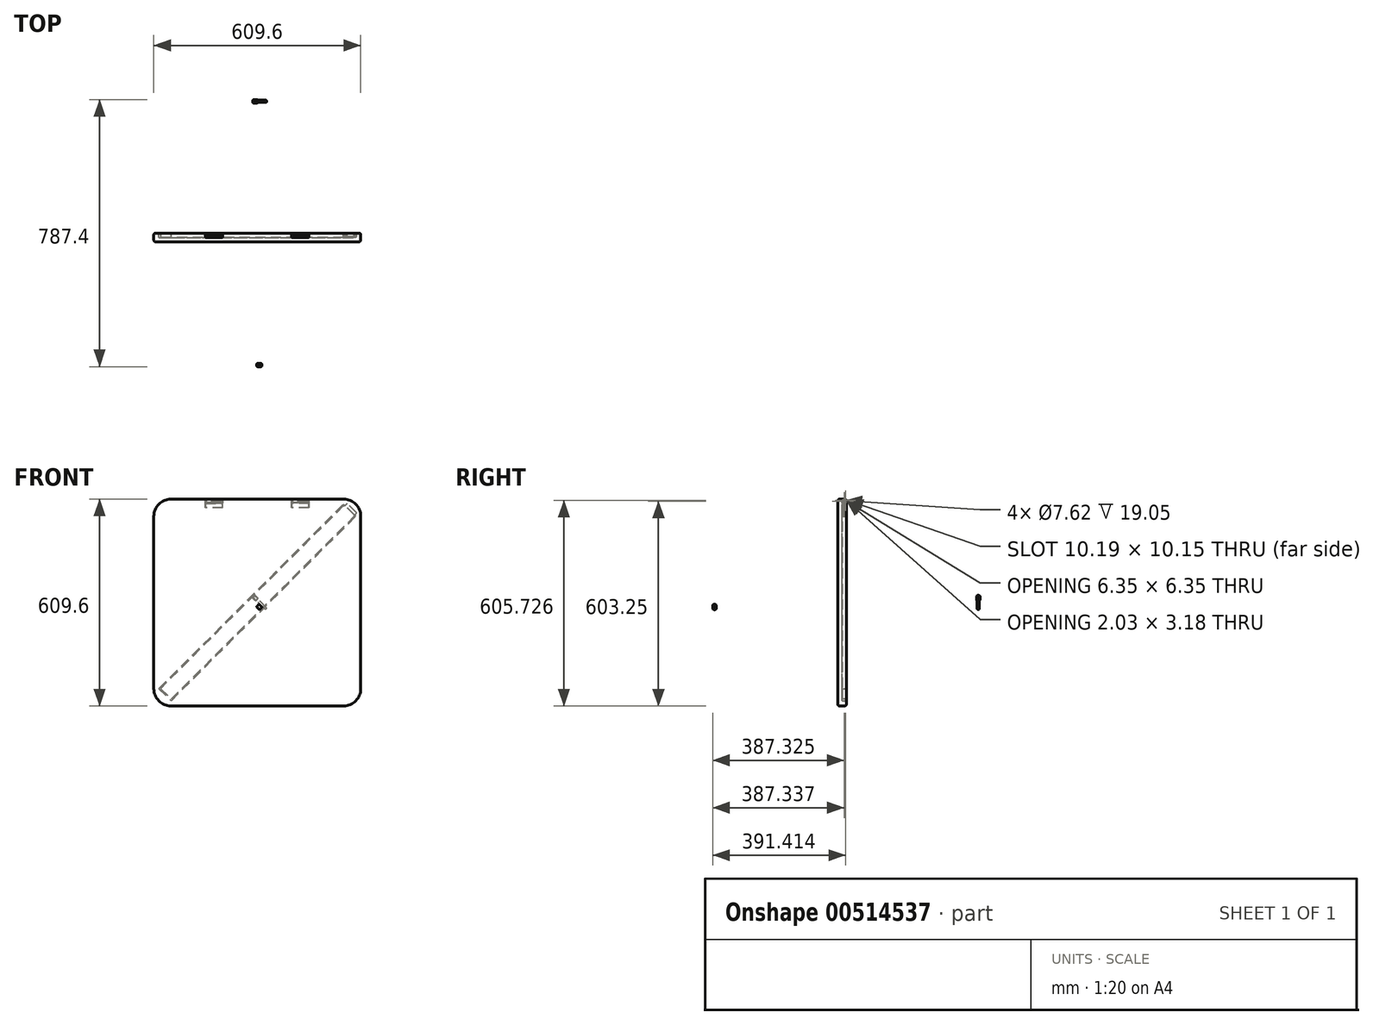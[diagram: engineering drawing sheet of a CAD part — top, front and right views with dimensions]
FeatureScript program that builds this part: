
annotation { "Feature Type Name" : "Feature", "Feature Type Description" : "" }
export const myFeature = defineFeature(function(context is Context, id is Id, definition is map)
    precondition{}
    {
        {
            var Q0;
            Q0=qCreatedBy(makeId("Front.planeOp"),FACE);
            var sketch = newSketch(context, id + "F0", { "sketchPlane" : qUnion([Q0])});
            skLineSegment(sketch, "E0.bottom", {"start": v(304.8, 304.8) * mm, "end": v(-304.8, 304.8) * mm});
            skLineSegment(sketch, "E0.top", {"start": v(304.8, -304.8) * mm, "end": v(-304.8, -304.8) * mm});
            skLineSegment(sketch, "E0.left", {"start": v(304.8, 304.8) * mm, "end": v(304.8, -304.8) * mm});
            skLineSegment(sketch, "E0.right", {"start": v(-304.8, 304.8) * mm, "end": v(-304.8, -304.8) * mm});
            skPoint(sketch, "E0.middle", {"position": v(0, 0) * mm});
            skSolve(sketch);
        }
        {
            var Q0;
            Q0=makeQuery(id+"F0.imprint","IMPRINT",FACE,{"disambiguationData":[TD([[makeQuery(id+"F0.imprint","IMPRINT",EDGE,{"derivedFrom":sQuery(id+"F0.wireOp",EDGE,"E0.bottom")}),1.0]])]});
            extrude(context, id + "F1", {"entities" : qUnion([Q0]), "depth" : 25.4 * mm, "offsetDistance" : 25.4 * mm});
        }
        {
            var Q0;
            Q0=makeQuery(id+"F1.opExtrude","SWEPT_EDGE",EDGE,{"disambiguationData":[OSD([sQuery(id+"F0.wireOp",EDGE,"E0.bottom"),sQuery(id+"F0.wireOp",EDGE,"E0.left")])]});
            var Q1;
            Q1=makeQuery(id+"F1.opExtrude","SWEPT_EDGE",EDGE,{"disambiguationData":[OSD([sQuery(id+"F0.wireOp",EDGE,"E0.bottom"),sQuery(id+"F0.wireOp",EDGE,"E0.right")])]});
            var Q2;
            Q2=makeQuery(id+"F1.opExtrude","SWEPT_EDGE",EDGE,{"disambiguationData":[OSD([sQuery(id+"F0.wireOp",EDGE,"E0.top"),sQuery(id+"F0.wireOp",EDGE,"E0.right")])]});
            var Q3;
            Q3=makeQuery(id+"F1.opExtrude","SWEPT_EDGE",EDGE,{"disambiguationData":[OSD([sQuery(id+"F0.wireOp",EDGE,"E0.top"),sQuery(id+"F0.wireOp",EDGE,"E0.left")])]});
            fillet(context, id + "F2", {"entities" : qUnion([Q0, Q1, Q2, Q3]), "radius" : 50.8 * mm, "tangentPropagation" : true, "allowEdgeOverflow" : false});
        }
        {
            var Q0;
            Q0=makeQuery(id+"F1.opExtrude","SWEPT_FACE",FACE,{"disambiguationData":[OSD([sQuery(id+"F0.wireOp",EDGE,"E0.bottom")])]});
            var sketch = newSketch(context, id + "F3", { "sketchPlane" : qUnion([Q0])});
            skLineSegment(sketch, "E1.bottom", {"start": v(-101.6, 12.7) * mm, "end": v(-152.4, 12.7) * mm});
            skLineSegment(sketch, "E1.top", {"start": v(-101.6, -12.7) * mm, "end": v(-152.4, -12.7) * mm});
            skLineSegment(sketch, "E1.left", {"start": v(-101.6, 12.7) * mm, "end": v(-101.6, -12.7) * mm});
            skLineSegment(sketch, "E1.right", {"start": v(-152.4, 12.7) * mm, "end": v(-152.4, -12.7) * mm});
            skPoint(sketch, "E1.middle", {"position": v(-127, 0) * mm});
            skLineSegment(sketch, "E2", {"start": v(-152.4, 0) * mm, "end": v(-152.4, 0) * mm});
            skLineSegment(sketch, "E3", {"start": v(0, 0) * mm, "end": v(-127, 0) * mm});
            skLineSegment(sketch, "E4", {"start": v(0, 0) * mm, "end": v(127, 0) * mm});
            skLineSegment(sketch, "E5.bottom", {"start": v(152.4, 12.7) * mm, "end": v(101.6, 12.7) * mm});
            skLineSegment(sketch, "E5.top", {"start": v(152.4, -12.7) * mm, "end": v(101.6, -12.7) * mm});
            skLineSegment(sketch, "E5.left", {"start": v(152.4, 12.7) * mm, "end": v(152.4, -12.7) * mm});
            skLineSegment(sketch, "E5.right", {"start": v(101.6, 12.7) * mm, "end": v(101.6, -12.7) * mm});
            skPoint(sketch, "E5.middle", {"position": v(127, 0) * mm});
            skSolve(sketch);
        }
        {
            var Q0;
            {var subQ6=sQuery(id+"F3.wireOp",EDGE,"E1.top");Q0=makeQuery(id+"F3.imprint","IMPRINT",FACE,{"disambiguationData":[TD([[makeQuery(id+"F3.imprint","IMPRINT",EDGE,{"derivedFrom":subQ6}),-1.0]])]});}
            var Q1;
            {var subQ1=sQuery(id+"F3.wireOp",EDGE,"E5.top");Q1=makeQuery(id+"F3.imprint","IMPRINT",FACE,{"disambiguationData":[TD([[makeQuery(id+"F3.imprint","IMPRINT",EDGE,{"derivedFrom":subQ1}),-1.0]])]});}
            extrude(context, id + "F4", {"entities" : qUnion([Q0, Q1]), "operationType" : NewBodyOperationType.REMOVE, "oppositeDirection" : true, "depth" : 12.7 * mm, "offsetDistance" : 25.4 * mm});
        }
        {
            var Q0;
            Q0=makeQuery(id+"F4.boolean.opBoolean","COPY",FACE,{"derivedFrom":makeQuery(id+"F4.opExtrude","SWEPT_FACE",FACE,{"disambiguationData":[OSD([sQuery(id+"F3.wireOp",EDGE,"E1.right")])]})});
            var sketch = newSketch(context, id + "F5", { "sketchPlane" : qUnion([Q0])});
            skLineSegment(sketch, "E6", {"start": v(-12.7, 298.45) * mm, "end": v(-6.38, 298.45) * mm});
            skPoint(sketch, "E6.endSnap0", {"position": v(-6.38, 304.8) * mm});
            skCircle(sketch, "E7", {"center": v(-6.38, 298.45) * mm, "radius": 5.08 * mm});
            skCircle(sketch, "E8", {"center": v(-6.38, 298.45) * mm, "radius": 3.81 * mm});
            skCircle(sketch, "E9", {"center": v(-6.38, 298.45) * mm, "radius": 3.18 * mm});
            skSolve(sketch);
        }
        {
            var Q0;
            Q0=makeQuery(id+"F5.imprint","IMPRINT",FACE,{"disambiguationData":[TD([[makeQuery(id+"F5.imprint","IMPRINT",EDGE,{"derivedFrom":sQuery(id+"F5.wireOp",EDGE,"E9")}),1.0]])]});
            extrude(context, id + "F6", {"entities" : qUnion([Q0]), "operationType" : NewBodyOperationType.ADD, "depth" : 50.8 * mm, "offsetDistance" : 25.4 * mm});
        }
        {
            var Q0;
            Q0=makeQuery(id+"F5.imprint","IMPRINT",FACE,{"disambiguationData":[TD([[makeQuery(id+"F5.imprint","IMPRINT",EDGE,{"derivedFrom":sQuery(id+"F5.wireOp",EDGE,"E7")}),1.0]])]});
            extrude(context, id + "F7", {"entities" : qUnion([Q0]), "operationType" : NewBodyOperationType.ADD, "depth" : 19.05 * mm, "offsetDistance" : 25.4 * mm});
        }
        {
            var Q0;
            Q0=makeQuery(id+"F4.boolean.opBoolean","COPY",FACE,{"derivedFrom":makeQuery(id+"F4.opExtrude","SWEPT_FACE",FACE,{"disambiguationData":[OSD([sQuery(id+"F3.wireOp",EDGE,"E1.left")])]})});
            var sketch = newSketch(context, id + "F8", { "sketchPlane" : qUnion([Q0])});
            skLineSegment(sketch, "E10", {"start": v(0, 298.45) * mm, "end": v(6.38, 298.45) * mm});
            skCircle(sketch, "E11", {"center": v(6.38, 298.45) * mm, "radius": 3.81 * mm});
            skCircle(sketch, "E12", {"center": v(6.38, 298.45) * mm, "radius": 5.08 * mm});
            skSolve(sketch);
        }
        {
            var Q0;
            Q0=makeQuery(id+"F8.imprint","IMPRINT",FACE,{"disambiguationData":[TD([[makeQuery(id+"F8.imprint","IMPRINT",EDGE,{"derivedFrom":sQuery(id+"F8.wireOp",EDGE,"E11")}),-1.0]])]});
            extrude(context, id + "F9", {"entities" : qUnion([Q0]), "operationType" : NewBodyOperationType.ADD, "depth" : 19.05 * mm, "offsetDistance" : 25.4 * mm});
        }
        {
            var Q0;
            Q0=makeQuery(id+"F4.boolean.opBoolean","COPY",FACE,{"derivedFrom":makeQuery(id+"F4.opExtrude","CAP_FACE",FACE,{"disambiguationData":[OSD([sQuery(id+"F0.wireOp",EDGE,"E0.bottom"),sQuery(id+"F3.wireOp",EDGE,"E1.top"),sQuery(id+"F3.wireOp",EDGE,"E1.left"),sQuery(id+"F3.wireOp",EDGE,"E1.right"),sQuery(id+"F3.wireOp",EDGE,"E3")])],"isStart":false})});
            var sketch = newSketch(context, id + "F10", { "sketchPlane" : qUnion([Q0])});
            skLineSegment(sketch, "E13.bottom", {"start": v(-152.4, 0) * mm, "end": v(-101.6, 0) * mm});
            skLineSegment(sketch, "E13.top", {"start": v(-152.4, -1.27) * mm, "end": v(-101.6, -1.27) * mm});
            skLineSegment(sketch, "E13.left", {"start": v(-152.4, 0) * mm, "end": v(-152.4, -1.27) * mm});
            skLineSegment(sketch, "E13.right", {"start": v(-101.6, 0) * mm, "end": v(-101.6, -1.27) * mm});
            skSolve(sketch);
        }
        {
            var Q0;
            Q0=makeQuery(id+"F10.imprint","IMPRINT",FACE,{"disambiguationData":[TD([[makeQuery(id+"F10.imprint","IMPRINT",EDGE,{"derivedFrom":sQuery(id+"F10.wireOp",EDGE,"E13.bottom")}),1.0]])]});
            extrude(context, id + "F11", {"entities" : qUnion([Q0]), "operationType" : NewBodyOperationType.REMOVE, "oppositeDirection" : true, "depth" : 12.7 * mm, "offsetDistance" : 25.4 * mm});
        }
        {
            var Q0;
            Q0=makeQuery(id+"F11.boolean.opBoolean","COPY",FACE,{"derivedFrom":makeQuery(id+"F11.opExtrude","SWEPT_FACE",FACE,{"disambiguationData":[OSD([sQuery(id+"F10.wireOp",EDGE,"E13.top")])]})});
            var sketch = newSketch(context, id + "F12", { "sketchPlane" : qUnion([Q0])});
            skLineSegment(sketch, "E14.bottom", {"start": v(101.85, 279.65) * mm, "end": v(152.15, 279.65) * mm});
            skLineSegment(sketch, "E14.top", {"start": v(101.85, 302.26) * mm, "end": v(152.15, 302.26) * mm});
            skLineSegment(sketch, "E14.left", {"start": v(101.85, 279.65) * mm, "end": v(101.85, 302.26) * mm});
            skLineSegment(sketch, "E14.right", {"start": v(152.15, 279.65) * mm, "end": v(152.15, 302.26) * mm});
            skLineSegment(sketch, "E15", {"start": v(127.47, 279.4) * mm, "end": v(127.47, 279.65) * mm});
            skSolve(sketch);
        }
        {
            var Q0;
            Q0 = qSketchRegion(id + "F12", true);
            extrude(context, id + "F13", {"entities" : qUnion([Q0]), "operationType" : NewBodyOperationType.ADD, "depth" : 1.27 * mm, "offsetDistance" : 25.4 * mm});
        }
        {
            var Q0;
            Q0=makeQuery(id+"F13.opExtrude","CAP_EDGE",EDGE,{"disambiguationData":[OSD([sQuery(id+"F12.wireOp",EDGE,"E14.top")])],"isStart":false});
            fillet(context, id + "F14", {"entities" : qUnion([Q0]), "radius" : 2.54 * mm, "tangentPropagation" : true, "allowEdgeOverflow" : false});
        }
        {
            var Q0;
            Q0=makeQuery(id+"F1.opExtrude","CAP_EDGE",EDGE,{"disambiguationData":[OSD([sQuery(id+"F0.wireOp",EDGE,"E0.right")])],"isStart":true});
            var Q1;
            Q1=makeQuery(id+"F1.opExtrude","CAP_EDGE",EDGE,{"disambiguationData":[OSD([sQuery(id+"F0.wireOp",EDGE,"E0.right")])],"isStart":false});
            var Q2;
            {var subQ0=sQuery(id+"F0.wireOp",EDGE,"E0.right");var subQ1=sQuery(id+"F0.wireOp",EDGE,"E0.bottom");Q2=makeQuery(id+"F2.opFillet","BLEND_EDGE",EDGE,{"blendedFrom":[makeQuery(id+"F1.opExtrude","SWEPT_EDGE",EDGE,{"disambiguationData":[OSD([subQ1,subQ0])]}),makeQuery(id+"F1.opExtrude","CAP_FACE",FACE,{"disambiguationData":[OSD([subQ1,sQuery(id+"F0.wireOp",EDGE,"E0.top"),sQuery(id+"F0.wireOp",EDGE,"E0.left"),subQ0])],"isStart":false})],"blendedInto":[makeQuery(id+"F1.opExtrude","CAP_FACE",FACE,{"disambiguationData":[OSD([subQ1,sQuery(id+"F0.wireOp",EDGE,"E0.top"),sQuery(id+"F0.wireOp",EDGE,"E0.left"),subQ0])],"isStart":false})]});}
            var Q3;
            {var subQ0=sQuery(id+"F0.wireOp",EDGE,"E0.right");var subQ1=sQuery(id+"F0.wireOp",EDGE,"E0.bottom");Q3=makeQuery(id+"F2.opFillet","BLEND_EDGE",EDGE,{"blendedFrom":[makeQuery(id+"F1.opExtrude","SWEPT_EDGE",EDGE,{"disambiguationData":[OSD([subQ1,subQ0])]}),makeQuery(id+"F1.opExtrude","CAP_FACE",FACE,{"disambiguationData":[OSD([subQ1,sQuery(id+"F0.wireOp",EDGE,"E0.top"),sQuery(id+"F0.wireOp",EDGE,"E0.left"),subQ0])],"isStart":true})],"blendedInto":[makeQuery(id+"F1.opExtrude","CAP_FACE",FACE,{"disambiguationData":[OSD([subQ1,sQuery(id+"F0.wireOp",EDGE,"E0.top"),sQuery(id+"F0.wireOp",EDGE,"E0.left"),subQ0])],"isStart":true})]});}
            var Q4;
            {var subQ0=sQuery(id+"F0.wireOp",EDGE,"E0.bottom");Q4=makeQuery(id+"F4.boolean.opBoolean","SPLIT",EDGE,{"disambiguationData":[TD([makeQuery(id+"F4.opExtrude","SWEPT_FACE",FACE,{"disambiguationData":[OSD([sQuery(id+"F3.wireOp",EDGE,"E1.left")])]})])],"derivedFrom":makeQuery(id+"F1.opExtrude","CAP_EDGE",EDGE,{"disambiguationData":[OSD([subQ0])],"isStart":true})});}
            fillet(context, id + "F15", {"entities" : qUnion([Q0, Q1, Q2, Q3, Q4]), "radius" : 5.08 * mm, "tangentPropagation" : true, "allowEdgeOverflow" : false});
        }
        {
            var Q0;
            Q0=makeQuery(id+"F4.boolean.opBoolean","COPY",FACE,{"derivedFrom":makeQuery(id+"F4.opExtrude","SWEPT_FACE",FACE,{"disambiguationData":[OSD([sQuery(id+"F3.wireOp",EDGE,"E5.right")])]})});
            var sketch = newSketch(context, id + "F16", { "sketchPlane" : qUnion([Q0])});
            skLineSegment(sketch, "E16", {"start": v(-12.7, 298.45) * mm, "end": v(-6.38, 298.45) * mm});
            skCircle(sketch, "E17", {"center": v(-6.38, 298.45) * mm, "radius": 5.08 * mm});
            skCircle(sketch, "E18", {"center": v(-6.38, 298.45) * mm, "radius": 3.81 * mm});
            skCircle(sketch, "E19", {"center": v(-6.38, 298.45) * mm, "radius": 3.18 * mm});
            skSolve(sketch);
        }
        {
            var Q0;
            Q0=makeQuery(id+"F16.imprint","IMPRINT",FACE,{"disambiguationData":[TD([[makeQuery(id+"F16.imprint","IMPRINT",EDGE,{"derivedFrom":sQuery(id+"F16.wireOp",EDGE,"E19")}),1.0]])]});
            extrude(context, id + "F17", {"entities" : qUnion([Q0]), "operationType" : NewBodyOperationType.ADD, "depth" : 50.8 * mm, "offsetDistance" : 25.4 * mm});
        }
        {
            var Q0;
            Q0=makeQuery(id+"F16.imprint","IMPRINT",FACE,{"disambiguationData":[TD([[makeQuery(id+"F16.imprint","IMPRINT",EDGE,{"derivedFrom":sQuery(id+"F16.wireOp",EDGE,"E17")}),1.0]])]});
            extrude(context, id + "F18", {"entities" : qUnion([Q0]), "operationType" : NewBodyOperationType.ADD, "depth" : 19.05 * mm, "offsetDistance" : 25.4 * mm});
        }
        {
            var Q0;
            Q0=makeQuery(id+"F4.boolean.opBoolean","COPY",FACE,{"derivedFrom":makeQuery(id+"F4.opExtrude","SWEPT_FACE",FACE,{"disambiguationData":[OSD([sQuery(id+"F3.wireOp",EDGE,"E5.left")])]})});
            var sketch = newSketch(context, id + "F19", { "sketchPlane" : qUnion([Q0])});
            skLineSegment(sketch, "E20", {"start": v(12.7, 298.45) * mm, "end": v(6.38, 298.45) * mm});
            skCircle(sketch, "E21", {"center": v(6.38, 298.45) * mm, "radius": 3.81 * mm});
            skCircle(sketch, "E22", {"center": v(6.38, 298.45) * mm, "radius": 5.08 * mm});
            skSolve(sketch);
        }
        {
            var Q0;
            Q0=makeQuery(id+"F19.imprint","IMPRINT",FACE,{"disambiguationData":[TD([[makeQuery(id+"F19.imprint","IMPRINT",EDGE,{"derivedFrom":sQuery(id+"F19.wireOp",EDGE,"E21")}),-1.0]])]});
            extrude(context, id + "F20", {"entities" : qUnion([Q0]), "operationType" : NewBodyOperationType.ADD, "depth" : 19.05 * mm, "offsetDistance" : 25.4 * mm});
        }
        {
            var Q0;
            Q0=makeQuery(id+"F1.opExtrude","CAP_FACE",FACE,{"disambiguationData":[OSD([sQuery(id+"F0.wireOp",EDGE,"E0.bottom"),sQuery(id+"F0.wireOp",EDGE,"E0.top"),sQuery(id+"F0.wireOp",EDGE,"E0.left"),sQuery(id+"F0.wireOp",EDGE,"E0.right")])],"isStart":true});
            var sketch = newSketch(context, id + "F21", { "sketchPlane" : qUnion([Q0])});
            skLineSegment(sketch, "E23.bottom", {"start": v(-152.4, 292.1) * mm, "end": v(-101.6, 292.1) * mm});
            skLineSegment(sketch, "E23.top", {"start": v(-152.4, 279.4) * mm, "end": v(-101.6, 279.4) * mm});
            skLineSegment(sketch, "E23.left", {"start": v(-152.4, 292.1) * mm, "end": v(-152.4, 279.4) * mm});
            skLineSegment(sketch, "E23.right", {"start": v(-101.6, 292.1) * mm, "end": v(-101.6, 279.4) * mm});
            skSolve(sketch);
        }
        {
            var Q0;
            Q0=makeQuery(id+"F21.imprint","IMPRINT",FACE,{"disambiguationData":[TD([[makeQuery(id+"F21.imprint","IMPRINT",EDGE,{"derivedFrom":sQuery(id+"F21.wireOp",EDGE,"E23.bottom")}),-1.0]])]});
            extrude(context, id + "F22", {"entities" : qUnion([Q0]), "operationType" : NewBodyOperationType.REMOVE, "oppositeDirection" : true, "depth" : 1.27 * mm, "offsetDistance" : 25.4 * mm});
        }
        {
            var Q0;
            Q0=makeQuery(id+"F22.boolean.opBoolean","COPY",FACE,{"derivedFrom":makeQuery(id+"F22.opExtrude","CAP_FACE",FACE,{"disambiguationData":[OSD([sQuery(id+"F21.wireOp",EDGE,"E23.bottom"),sQuery(id+"F21.wireOp",EDGE,"E23.top"),sQuery(id+"F21.wireOp",EDGE,"E23.left"),sQuery(id+"F21.wireOp",EDGE,"E23.right")])],"isStart":false})});
            var sketch = newSketch(context, id + "F23", { "sketchPlane" : qUnion([Q0])});
            skLineSegment(sketch, "E24.bottom", {"start": v(-152.15, 279.65) * mm, "end": v(-101.85, 279.65) * mm});
            skLineSegment(sketch, "E24.top", {"start": v(-152.15, 302.51) * mm, "end": v(-101.85, 302.51) * mm});
            skLineSegment(sketch, "E24.left", {"start": v(-152.15, 279.65) * mm, "end": v(-152.15, 302.51) * mm});
            skLineSegment(sketch, "E24.right", {"start": v(-101.85, 279.65) * mm, "end": v(-101.85, 302.51) * mm});
            skSolve(sketch);
        }
        {
            var Q0;
            Q0 = qSketchRegion(id + "F23", true);
            extrude(context, id + "F24", {"entities" : qUnion([Q0]), "operationType" : NewBodyOperationType.ADD, "depth" : 1.27 * mm, "offsetDistance" : 25.4 * mm});
        }
        {
            var Q0;
            Q0=makeQuery(id+"F24.opExtrude","CAP_EDGE",EDGE,{"disambiguationData":[OSD([sQuery(id+"F23.wireOp",EDGE,"E24.top")])],"isStart":false});
            fillet(context, id + "F25", {"entities" : qUnion([Q0]), "radius" : 2.54 * mm, "tangentPropagation" : true, "allowEdgeOverflow" : false});
        }
        {
            var Q0;
            Q0=makeQuery(id+"F16.imprint","IMPRINT",FACE,{"disambiguationData":[TD([[makeQuery(id+"F16.imprint","IMPRINT",EDGE,{"derivedFrom":sQuery(id+"F16.wireOp",EDGE,"E17")}),-1.0]])]});
            var sketch = newSketch(context, id + "F26", { "sketchPlane" : qUnion([Q0])});
            skLineSegment(sketch, "E25", {"start": v(-1.27, 302.51) * mm, "end": v(-3.3, 302.51) * mm});
            skArc(sketch, "E26", {"start": v(-1.27, 299.34) * mm, "mid": v(-1.98, 301.12) * mm, "end": v(-3.3, 302.51) * mm});
            skLineSegment(sketch, "E27", {"start": v(-1.27, 299.34) * mm, "end": v(-1.27, 302.51) * mm});
            skSolve(sketch);
        }
        {
            var Q0;
            Q0=makeQuery(id+"F26.imprint","IMPRINT",FACE,{"disambiguationData":[TD([[makeQuery(id+"F26.imprint","IMPRINT",EDGE,{"derivedFrom":sQuery(id+"F26.wireOp",EDGE,"E25")}),1.0]])]});
            extrude(context, id + "F27", {"entities" : qUnion([Q0]), "operationType" : NewBodyOperationType.ADD, "depth" : 50.8 * mm, "offsetDistance" : 25.4 * mm});
        }
        {
            var Q0;
            Q0=makeQuery(id+"F5.imprint","IMPRINT",FACE,{"disambiguationData":[TD([[makeQuery(id+"F5.imprint","IMPRINT",EDGE,{"derivedFrom":sQuery(id+"F5.wireOp",EDGE,"E7")}),-1.0]])]});
            var sketch = newSketch(context, id + "F28", { "sketchPlane" : qUnion([Q0])});
            skLineSegment(sketch, "E28", {"start": v(-1.27, 302.26) * mm, "end": v(-3.05, 302.26) * mm});
            skLineSegment(sketch, "E29", {"start": v(-1.27, 302.26) * mm, "end": v(-1.27, 299.09) * mm});
            skArc(sketch, "E30", {"start": v(-1.27, 299.09) * mm, "mid": v(-1.86, 300.84) * mm, "end": v(-3.05, 302.26) * mm});
            skSolve(sketch);
        }
        {
            var Q0;
            Q0 = qSketchRegion(id + "F28", true);
            extrude(context, id + "F29", {"entities" : qUnion([Q0]), "operationType" : NewBodyOperationType.ADD, "depth" : 50.8 * mm, "offsetDistance" : 25.4 * mm});
        }
        {
            var Q0;
            Q0=makeQuery(id+"F1.opExtrude","CAP_FACE",FACE,{"disambiguationData":[OSD([sQuery(id+"F0.wireOp",EDGE,"E0.bottom"),sQuery(id+"F0.wireOp",EDGE,"E0.top"),sQuery(id+"F0.wireOp",EDGE,"E0.left"),sQuery(id+"F0.wireOp",EDGE,"E0.right")])],"isStart":true});
            var sketch = newSketch(context, id + "F30", { "sketchPlane" : qUnion([Q0])});
            skLineSegment(sketch, "E31", {"start": v(-271.65, 271.65) * mm, "end": v(-253.7, 289.61) * mm});
            skLineSegment(sketch, "E32", {"start": v(-271.65, 271.65) * mm, "end": v(-289.61, 253.7) * mm});
            skLineSegment(sketch, "E33", {"start": v(271.65, -271.65) * mm, "end": v(289.61, -253.7) * mm});
            skLineSegment(sketch, "E34", {"start": v(271.65, -271.65) * mm, "end": v(253.7, -289.61) * mm});
            skLineSegment(sketch, "E35", {"start": v(289.61, -253.7) * mm, "end": v(-253.7, 289.61) * mm});
            skLineSegment(sketch, "E36", {"start": v(253.7, -289.61) * mm, "end": v(-289.61, 253.7) * mm});
            skLineSegment(sketch, "E37", {"start": v(-286.33, 286.33) * mm, "end": v(-271.65, 271.65) * mm});
            skLineSegment(sketch, "E38", {"start": v(271.65, -271.65) * mm, "end": v(286.33, -286.33) * mm});
            skSolve(sketch);
        }
        {
            var Q0;
            Q0=makeQuery(id+"F30.imprint","IMPRINT",FACE,{"disambiguationData":[TD([[makeQuery(id+"F30.imprint","IMPRINT",EDGE,{"derivedFrom":sQuery(id+"F30.wireOp",EDGE,"E31")}),-1.0]])]});
            extrude(context, id + "F31", {"entities" : qUnion([Q0]), "operationType" : NewBodyOperationType.REMOVE, "oppositeDirection" : true, "depth" : 12.7 * mm, "offsetDistance" : 25.4 * mm});
        }
        {
            var Q0;
            Q0=makeQuery(id+"F31.boolean.opBoolean","COPY",FACE,{"derivedFrom":makeQuery(id+"F31.opExtrude","CAP_FACE",FACE,{"disambiguationData":[OSD([sQuery(id+"F30.wireOp",EDGE,"E31"),sQuery(id+"F30.wireOp",EDGE,"E32"),sQuery(id+"F30.wireOp",EDGE,"E33"),sQuery(id+"F30.wireOp",EDGE,"E34"),sQuery(id+"F30.wireOp",EDGE,"E35"),sQuery(id+"F30.wireOp",EDGE,"E36")])],"isStart":false})});
            var sketch = newSketch(context, id + "F32", { "sketchPlane" : qUnion([Q0])});
            skLineSegment(sketch, "E39", {"start": v(-253.7, 285.12) * mm, "end": v(285.12, -253.7) * mm});
            skLineSegment(sketch, "E40", {"start": v(285.12, -253.7) * mm, "end": v(253.7, -285.12) * mm});
            skLineSegment(sketch, "E41", {"start": v(253.7, -285.12) * mm, "end": v(-285.12, 253.7) * mm});
            skLineSegment(sketch, "E42", {"start": v(-285.12, 253.7) * mm, "end": v(-253.7, 285.12) * mm});
            skLineSegment(sketch, "E43", {"start": v(-250.38, 281.8) * mm, "end": v(-248.13, 284.05) * mm});
            skLineSegment(sketch, "E44", {"start": v(-258.92, 279.9) * mm, "end": v(-261.16, 282.14) * mm});
            skLineSegment(sketch, "E45", {"start": v(-222.14, 190.7) * mm, "end": v(-224.38, 188.46) * mm});
            skLineSegment(sketch, "E46", {"start": v(270.67, -268.15) * mm, "end": v(272.92, -270.4) * mm});
            skSolve(sketch);
        }
        {
            var Q0;
            {var subQ4=sQuery(id+"F32.wireOp",EDGE,"E39");var subQ7=sQuery(id+"F32.wireOp",EDGE,"E42");var subQ8=makeQuery(id+"F32.imprint","INTERSECT",VERTEX,{"derivedFrom":[subQ4,subQ7]});Q0=makeQuery(id+"F32.imprint","IMPRINT",FACE,{"disambiguationData":[TD([[makeQuery(id+"F32.imprint","IMPRINT",EDGE,{"disambiguationData":[TD([[subQ8,-1.0]])],"derivedFrom":subQ4}),-1.0]])]});}
            extrude(context, id + "F33", {"entities" : qUnion([Q0]), "operationType" : NewBodyOperationType.ADD, "depth" : 12.7 * mm, "offsetDistance" : 25.4 * mm});
        }
        {
            var Q0;
            Q0=makeQuery(id+"F33.opExtrude","SWEPT_FACE",FACE,{"disambiguationData":[OSD([sQuery(id+"F32.wireOp",EDGE,"E42")])]});
            var sketch = newSketch(context, id + "F34", { "sketchPlane" : qUnion([Q0])});
            skLineSegment(sketch, "E47.bottom", {"start": v(0, -19.69) * mm, "end": v(-12.7, -19.69) * mm});
            skLineSegment(sketch, "E47.top", {"start": v(0, 19.69) * mm, "end": v(-12.7, 19.69) * mm});
            skLineSegment(sketch, "E47.left", {"start": v(0, -19.69) * mm, "end": v(0, 19.69) * mm});
            skLineSegment(sketch, "E47.right", {"start": v(-12.7, -19.69) * mm, "end": v(-12.7, 19.69) * mm});
            skSolve(sketch);
        }
        {
            var Q0;
            Q0=makeQuery(id+"F34.imprint","IMPRINT",FACE,{"disambiguationData":[TD([[makeQuery(id+"F34.imprint","IMPRINT",EDGE,{"derivedFrom":sQuery(id+"F34.wireOp",EDGE,"E47.bottom")}),-1.0]])]});
            extrude(context, id + "F35", {"entities" : qUnion([Q0]), "operationType" : NewBodyOperationType.ADD, "depth" : 2.54 * mm, "offsetDistance" : 25.4 * mm});
        }
        {
            var Q0;
            Q0=makeQuery(id+"F1.opExtrude","CAP_FACE",FACE,{"disambiguationData":[OSD([sQuery(id+"F0.wireOp",EDGE,"E0.bottom"),sQuery(id+"F0.wireOp",EDGE,"E0.top"),sQuery(id+"F0.wireOp",EDGE,"E0.left"),sQuery(id+"F0.wireOp",EDGE,"E0.right")])],"isStart":true});
            var sketch = newSketch(context, id + "F36", { "sketchPlane" : qUnion([Q0])});
            skLineSegment(sketch, "E48", {"start": v(-285.93, 258.1) * mm, "end": v(-258.1, 285.93) * mm});
            skLineSegment(sketch, "E49", {"start": v(-285.93, 258.1) * mm, "end": v(-292.49, 264.65) * mm});
            skLineSegment(sketch, "E50", {"start": v(-292.49, 264.65) * mm, "end": v(-264.65, 292.49) * mm});
            skLineSegment(sketch, "E51", {"start": v(-258.1, 285.93) * mm, "end": v(-264.65, 292.49) * mm});
            skLineSegment(sketch, "E52", {"start": v(-258.1, 285.93) * mm, "end": v(-257.28, 285.12) * mm});
            skLineSegment(sketch, "E53", {"start": v(-285.93, 258.1) * mm, "end": v(-285.12, 257.28) * mm});
            skSolve(sketch);
        }
        {
            var Q0;
            Q0=makeQuery(id+"F36.imprint","IMPRINT",FACE,{"disambiguationData":[TD([[makeQuery(id+"F36.imprint","IMPRINT",EDGE,{"derivedFrom":sQuery(id+"F36.wireOp",EDGE,"E48")}),1.0]])]});
            var Q1;
            {var subQ0=sQuery(id+"F36.wireOp",EDGE,"E48");Q1=makeQuery(id+"F36.imprint","IMPRINT",FACE,{"disambiguationData":[TD([[makeQuery(id+"F36.imprint","IMPRINT",EDGE,{"derivedFrom":subQ0}),-1.0]])]});}
            extrude(context, id + "F37", {"entities" : qUnion([Q0, Q1]), "operationType" : NewBodyOperationType.REMOVE, "oppositeDirection" : true, "depth" : 10.4 * mm, "offsetDistance" : 25.4 * mm});
        }
        {
            var Q0;
            Q0=makeQuery(id+"F37.boolean.opBoolean","COPY",FACE,{"derivedFrom":makeQuery(id+"F37.opExtrude","SWEPT_FACE",FACE,{"disambiguationData":[OSD([sQuery(id+"F36.wireOp",EDGE,"E51"),sQuery(id+"F36.wireOp",EDGE,"E52")])]})});
            var sketch = newSketch(context, id + "F38", { "sketchPlane" : qUnion([Q0])});
            skLineSegment(sketch, "E54", {"start": v(393.95, 5.2) * mm, "end": v(388.62, 5.2) * mm});
            skPoint(sketch, "E54.endSnap0", {"position": v(393.95, 5.2) * mm});
            skCircle(sketch, "E55", {"center": v(388.62, 5.2) * mm, "radius": 3.18 * mm});
            skCircle(sketch, "E56", {"center": v(388.62, 5.2) * mm, "radius": 3.81 * mm});
            skCircle(sketch, "E57", {"center": v(388.62, 5.2) * mm, "radius": 5.08 * mm});
            skSolve(sketch);
        }
        {
            var Q0;
            Q0=makeQuery(id+"F38.imprint","IMPRINT",FACE,{"disambiguationData":[TD([[makeQuery(id+"F38.imprint","IMPRINT",EDGE,{"derivedFrom":sQuery(id+"F38.wireOp",EDGE,"E55")}),1.0]])]});
            extrude(context, id + "F39", {"entities" : qUnion([Q0]), "operationType" : NewBodyOperationType.ADD, "depth" : 50.8 * mm, "offsetDistance" : 25.4 * mm});
        }
        {
            var Q0;
            Q0=makeQuery(id+"F37.boolean.opBoolean","COPY",FACE,{"derivedFrom":makeQuery(id+"F37.opExtrude","SWEPT_FACE",FACE,{"disambiguationData":[OSD([sQuery(id+"F36.wireOp",EDGE,"E49"),sQuery(id+"F36.wireOp",EDGE,"E53")])]})});
            var sketch = newSketch(context, id + "F40", { "sketchPlane" : qUnion([Q0])});
            skCircle(sketch, "E58", {"center": v(388.62, -5.2) * mm, "radius": 3.81 * mm});
            skCircle(sketch, "E59", {"center": v(388.62, -5.2) * mm, "radius": 5.08 * mm});
            skSolve(sketch);
        }
        {
            var Q0;
            Q0=makeQuery(id+"F40.imprint","IMPRINT",FACE,{"disambiguationData":[TD([[makeQuery(id+"F40.imprint","IMPRINT",EDGE,{"derivedFrom":sQuery(id+"F40.wireOp",EDGE,"E58")}),-1.0]])]});
            extrude(context, id + "F41", {"entities" : qUnion([Q0]), "operationType" : NewBodyOperationType.ADD, "depth" : 12.7 * mm, "offsetDistance" : 25.4 * mm});
        }
        {
            var Q0;
            Q0=makeQuery(id+"F38.imprint","IMPRINT",FACE,{"disambiguationData":[TD([[makeQuery(id+"F38.imprint","IMPRINT",EDGE,{"derivedFrom":sQuery(id+"F38.wireOp",EDGE,"E56")}),-1.0]])]});
            extrude(context, id + "F42", {"entities" : qUnion([Q0]), "operationType" : NewBodyOperationType.ADD, "depth" : 12.7 * mm, "offsetDistance" : 25.4 * mm});
        }
        {
            var Q0;
            Q0=makeQuery(id+"F35.opExtrude","CAP_FACE",FACE,{"disambiguationData":[OSD([sQuery(id+"F34.wireOp",EDGE,"E47.bottom"),sQuery(id+"F34.wireOp",EDGE,"E47.top"),sQuery(id+"F34.wireOp",EDGE,"E47.left"),sQuery(id+"F34.wireOp",EDGE,"E47.right")])],"isStart":false});
            extrude(context, id + "F43", {"entities" : qUnion([Q0]), "operationType" : NewBodyOperationType.ADD, "depth" : 1.27 * mm, "offsetDistance" : 25.4 * mm});
        }
    });
